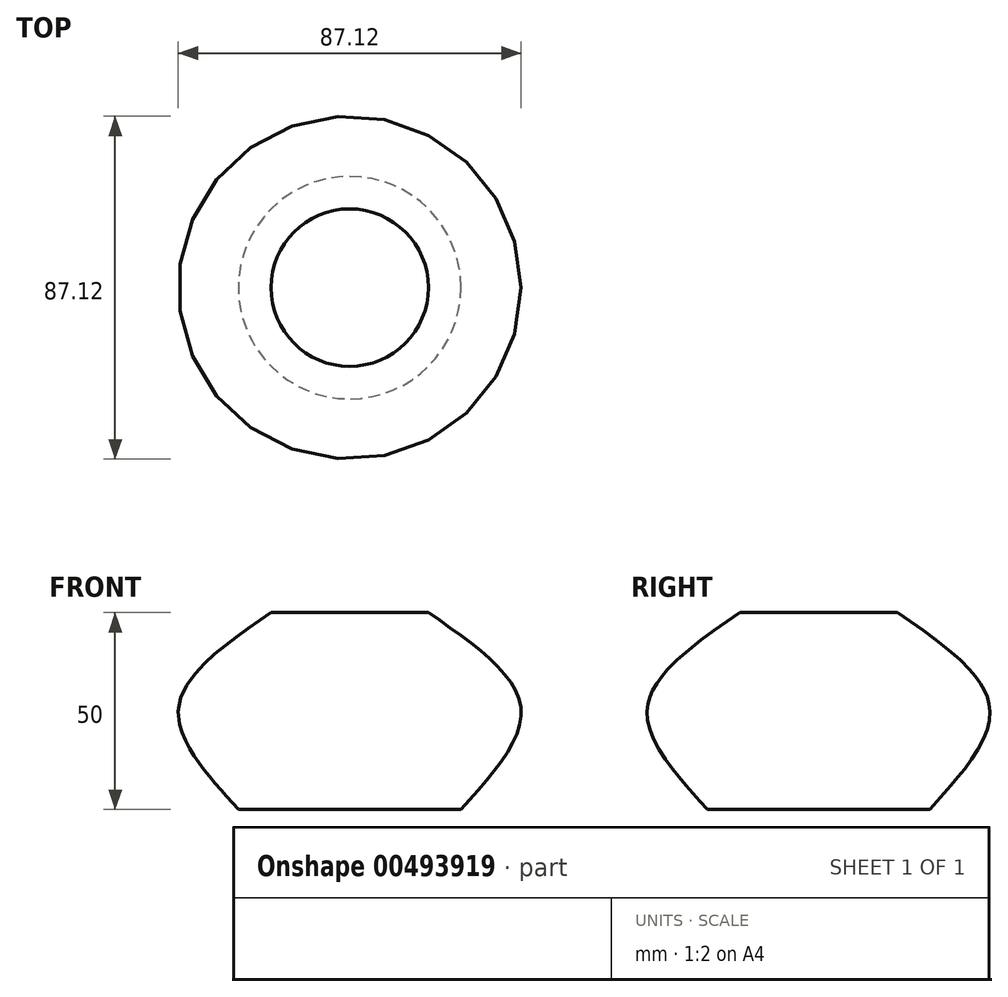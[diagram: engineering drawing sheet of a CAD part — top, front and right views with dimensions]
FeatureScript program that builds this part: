
annotation { "Feature Type Name" : "Feature", "Feature Type Description" : "" }
export const myFeature = defineFeature(function(context is Context, id is Id, definition is map)
    precondition{}
    {
        {
            var Q0;
            Q0=qCreatedBy(makeId("Top.planeOp"),FACE);
            cPlane(context, id + "F0", {"entities" : qUnion([Q0]), "cplaneType" : CPlaneType.OFFSET, "offset" : 25 * mm, "width" : 150 * mm, "height" : 150 * mm});
        }
        {
            var Q0;
            Q0=qCreatedBy(id+"F0.planeOp",FACE);
            cPlane(context, id + "F1", {"entities" : qUnion([Q0]), "cplaneType" : CPlaneType.OFFSET, "offset" : 25 * mm, "width" : 150 * mm, "height" : 150 * mm});
        }
        {
            var Q0;
            Q0=qCreatedBy(makeId("Top.planeOp"),FACE);
            var sketch = newSketch(context, id + "F2", { "sketchPlane" : qUnion([Q0])});
            skCircle(sketch, "E0", {"center": v(0, 0) * mm, "radius": 28.26 * mm});
            skSolve(sketch);
        }
        {
            var Q0;
            Q0=qCreatedBy(id+"F1.planeOp",FACE);
            var sketch = newSketch(context, id + "F3", { "sketchPlane" : qUnion([Q0])});
            skCircle(sketch, "E1", {"center": v(0, 0) * mm, "radius": 20 * mm});
            skSolve(sketch);
        }
        {
            var Q0;
            Q0=qCreatedBy(id+"F0.planeOp",FACE);
            var sketch = newSketch(context, id + "F4", { "sketchPlane" : qUnion([Q0])});
            skCircle(sketch, "E2", {"center": v(0, 0) * mm, "radius": 43.55 * mm});
            skSolve(sketch);
        }
        {
            var Q0;
            Q0=makeQuery(id+"F2.imprint","IMPRINT",FACE,{"disambiguationData":[TD([[makeQuery(id+"F2.imprint","IMPRINT",EDGE,{"derivedFrom":sQuery(id+"F2.wireOp",EDGE,"E0")}),1.0]])]});
            var Q1;
            Q1=makeQuery(id+"F4.imprint","IMPRINT",FACE,{"disambiguationData":[TD([[makeQuery(id+"F4.imprint","IMPRINT",EDGE,{"derivedFrom":sQuery(id+"F4.wireOp",EDGE,"E2")}),1.0]])]});
            var Q2;
            Q2=makeQuery(id+"F3.imprint","IMPRINT",FACE,{"disambiguationData":[TD([[makeQuery(id+"F3.imprint","IMPRINT",EDGE,{"derivedFrom":sQuery(id+"F3.wireOp",EDGE,"E1")}),1.0]])]});
            loft(context, id + "F5", {"sheetProfilesArray" : [{ "sheetProfileEntities" : qUnion([Q0]) }, { "sheetProfileEntities" : qUnion([Q1]) }, { "sheetProfileEntities" : qUnion([Q2]) }]});
        }
    });
